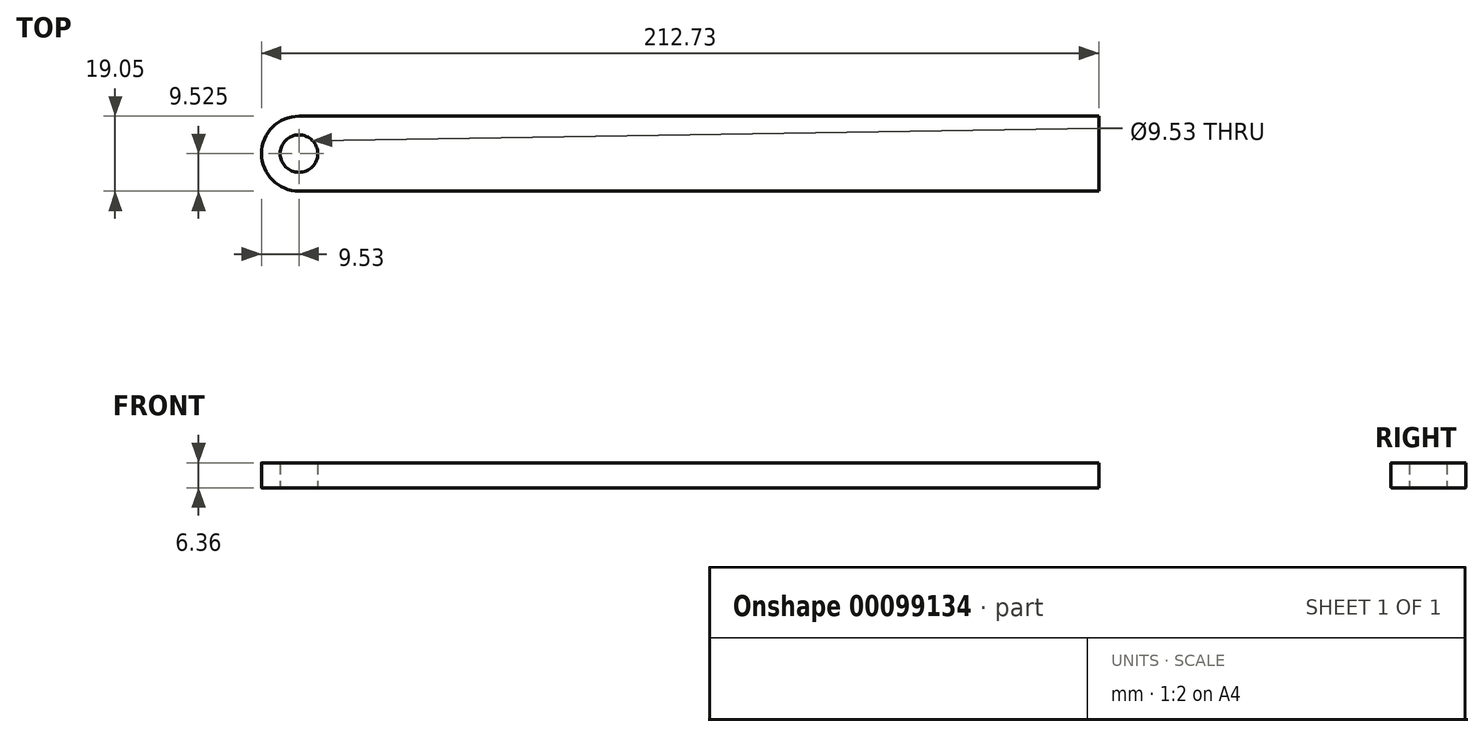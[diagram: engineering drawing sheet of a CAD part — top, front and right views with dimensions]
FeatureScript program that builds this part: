
annotation { "Feature Type Name" : "Feature", "Feature Type Description" : "" }
export const myFeature = defineFeature(function(context is Context, id is Id, definition is map)
    precondition{}
    {
        {
            var Q0;
            Q0=qCreatedBy(makeId("Top.planeOp"),FACE);
            var sketch = newSketch(context, id + "F0", { "sketchPlane" : qUnion([Q0])});
            skLineSegment(sketch, "E0", {"start": v(0, 0) * mm, "end": v(0, 19.05) * mm});
            skLineSegment(sketch, "E1", {"start": v(0, 19.05) * mm, "end": v(-203.2, 19.05) * mm});
            skLineSegment(sketch, "E2", {"start": v(0, 0) * mm, "end": v(-203.2, 0) * mm});
            skArc(sketch, "E3", {"start": v(-203.2, 19.05) * mm, "mid": v(-212.73, 9.52) * mm, "end": v(-203.2, 0) * mm});
            skCircle(sketch, "E4", {"center": v(-203.2, 9.52) * mm, "radius": 4.76 * mm});
            skSolve(sketch);
        }
        {
            assignVariable(context, id + "F1", {"name" : "FRadius", "anyValue" : .1});
        }
        {
            var Q0;
            Q0=qSketchRegion(id+"F0",true);
            extrude(context, id + "F2", {"entities" : qUnion([Q0]), "endBound" : BoundingType.SYMMETRIC, "depth" : 6.35 * mm});
        }
        {
            var Q0;
            Q0=makeQuery(id+"F2.opExtrude","CAP_EDGE",EDGE,{"disambiguationData":[OSD([sQuery(id+"F0.wireOp",EDGE,"E2")])],"isStart":false});
            var Q1;
            Q1=makeQuery(id+"F2.opExtrude","CAP_EDGE",EDGE,{"disambiguationData":[OSD([sQuery(id+"F0.wireOp",EDGE,"E2")])],"isStart":true});
            fillet(context, id + "F3", {"entities" : qUnion([Q0, Q1]), "radius" : (getVariable(context, 'FRadius')) * mm, "tangentPropagation" : true, "allowEdgeOverflow" : false});
        }
    });
